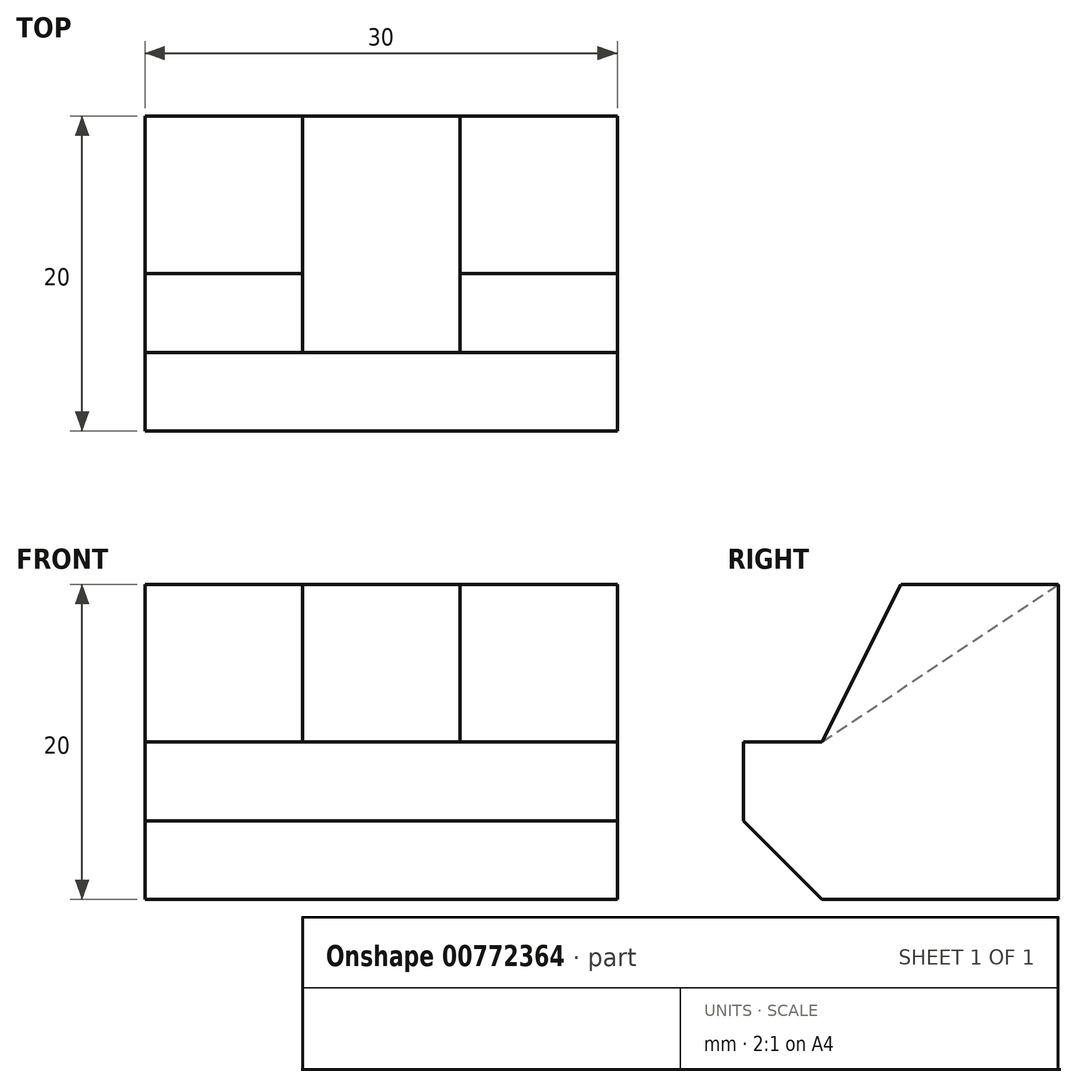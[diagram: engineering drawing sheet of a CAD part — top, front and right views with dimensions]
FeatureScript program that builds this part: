
annotation { "Feature Type Name" : "Feature", "Feature Type Description" : "" }
export const myFeature = defineFeature(function(context is Context, id is Id, definition is map)
    precondition{}
    {
        {
            var Q0;
            Q0=qCreatedBy(makeId("Right.planeOp"),FACE);
            var sketch = newSketch(context, id + "F0", { "sketchPlane" : qUnion([Q0])});
            skLineSegment(sketch, "E0", {"start": v(0, 0) * mm, "end": v(-15, 0) * mm});
            skLineSegment(sketch, "E1", {"start": v(-15, 0) * mm, "end": v(-20, 5) * mm});
            skLineSegment(sketch, "E2", {"start": v(-20, 5) * mm, "end": v(-20, 10) * mm});
            skLineSegment(sketch, "E3", {"start": v(-20, 10) * mm, "end": v(-15, 10) * mm});
            skLineSegment(sketch, "E4", {"start": v(-15, 10) * mm, "end": v(-10, 20) * mm});
            skLineSegment(sketch, "E5", {"start": v(-10, 20) * mm, "end": v(0, 20) * mm});
            skLineSegment(sketch, "E6", {"start": v(0, 20) * mm, "end": v(0, 0) * mm});
            skLineSegment(sketch, "E7", {"start": v(-15, 10) * mm, "end": v(0, 20) * mm});
            skSolve(sketch);
        }
        {
            var Q0;
            Q0 = qSketchRegion(id + "F0", true);
            extrude(context, id + "F1", {"entities" : qUnion([Q0]), "endBound" : BoundingType.SYMMETRIC, "depth" : 30 * mm, "offsetDistance" : 25 * mm});
        }
        {
            var Q0;
            Q0=makeQuery(id+"F0.imprint","IMPRINT",FACE,{"disambiguationData":[TD([[makeQuery(id+"F0.imprint","IMPRINT",EDGE,{"derivedFrom":sQuery(id+"F0.wireOp",EDGE,"E4")}),-1.0]])]});
            extrude(context, id + "F2", {"entities" : qUnion([Q0]), "operationType" : NewBodyOperationType.REMOVE, "endBound" : BoundingType.SYMMETRIC, "oppositeDirection" : true, "depth" : 10 * mm, "offsetDistance" : 25 * mm});
        }
    });
